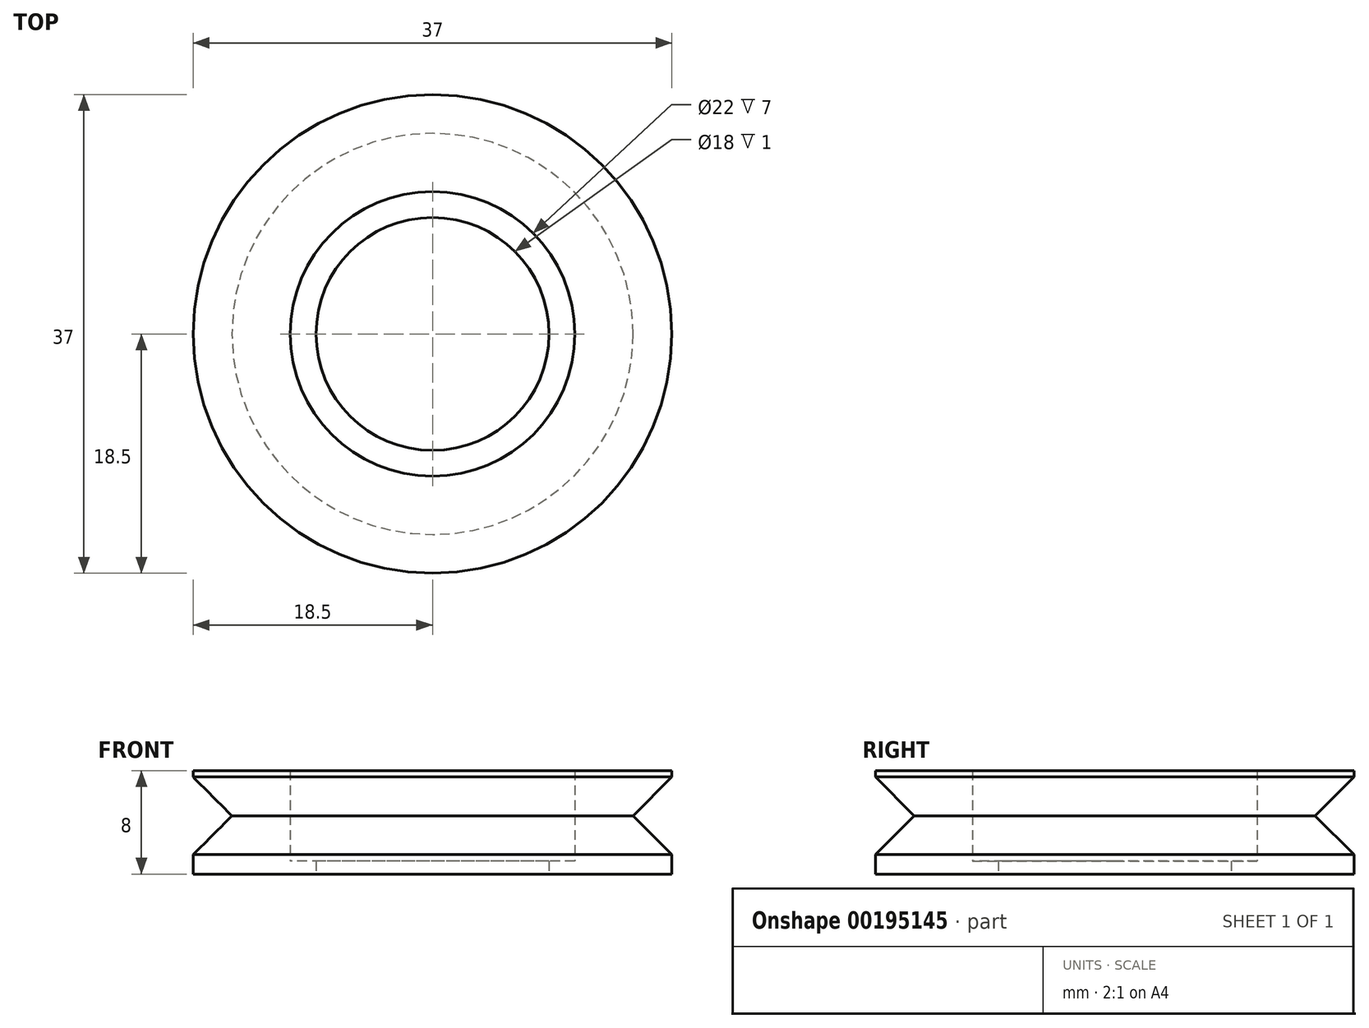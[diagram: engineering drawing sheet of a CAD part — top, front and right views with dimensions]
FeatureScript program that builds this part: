
annotation { "Feature Type Name" : "Feature", "Feature Type Description" : "" }
export const myFeature = defineFeature(function(context is Context, id is Id, definition is map)
    precondition{}
    {
        {
            var Q0;
            Q0=qCreatedBy(makeId("Top.planeOp"),FACE);
            var sketch = newSketch(context, id + "F0", { "sketchPlane" : qUnion([Q0])});
            skCircle(sketch, "E0", {"center": v(0, 0) * mm, "radius": 11 * mm});
            skCircle(sketch, "E1", {"center": v(0, 0) * mm, "radius": 18.5 * mm});
            skSolve(sketch);
        }
        {
            var Q0;
            Q0=makeQuery(id+"F0.imprint","IMPRINT",FACE,{"disambiguationData":[TD([[makeQuery(id+"F0.imprint","IMPRINT",EDGE,{"derivedFrom":sQuery(id+"F0.wireOp",EDGE,"E0")}),-1.0]])]});
            extrude(context, id + "F1", {"entities" : qUnion([Q0]), "depth" : 7 * mm});
        }
        {
            var Q0;
            Q0=makeQuery(id+"F0.imprint","IMPRINT",FACE,{"disambiguationData":[TD([[makeQuery(id+"F0.imprint","IMPRINT",EDGE,{"derivedFrom":sQuery(id+"F0.wireOp",EDGE,"E0")}),1.0]])]});
            var Q1;
            Q1=makeQuery(id+"F0.imprint","IMPRINT",FACE,{"disambiguationData":[TD([[makeQuery(id+"F0.imprint","IMPRINT",EDGE,{"derivedFrom":sQuery(id+"F0.wireOp",EDGE,"E0")}),-1.0]])]});
            extrude(context, id + "F2", {"entities" : qUnion([Q0, Q1]), "operationType" : NewBodyOperationType.ADD, "oppositeDirection" : true, "depth" : 1 * mm});
        }
        {
            var Q0;
            Q0=makeQuery(id+"F2.opExtrude","CAP_FACE",FACE,{"disambiguationData":[OSD([sQuery(id+"F0.wireOp",EDGE,"E1")])],"isStart":false});
            var sketch = newSketch(context, id + "F3", { "sketchPlane" : qUnion([Q0])});
            skCircle(sketch, "E2", {"center": v(0, 0) * mm, "radius": 9 * mm});
            skSolve(sketch);
        }
        {
            var Q0;
            Q0=makeQuery(id+"F3.imprint","IMPRINT",FACE,{"disambiguationData":[TD([[makeQuery(id+"F3.imprint","IMPRINT",EDGE,{"derivedFrom":sQuery(id+"F3.wireOp",EDGE,"E2")}),1.0]])]});
            extrude(context, id + "F4", {"entities" : qUnion([Q0]), "operationType" : NewBodyOperationType.REMOVE, "oppositeDirection" : true, "depth" : 25 * mm});
        }
        {
            var Q0;
            Q0=qCreatedBy(makeId("Front.planeOp"),FACE);
            var sketch = newSketch(context, id + "F5", { "sketchPlane" : qUnion([Q0])});
            skLineSegment(sketch, "E3", {"start": v(0, 8.94) * mm, "end": v(0, -2.8) * mm, "construction": true});
            skLineSegment(sketch, "E4", {"start": v(-18.5, -1) * mm, "end": v(-18.5, 7) * mm});
            skLineSegment(sketch, "E5", {"start": v(-15.5, 3.5) * mm, "end": v(-18.5, 6.5) * mm});
            skLineSegment(sketch, "E6", {"start": v(-15.5, 3.5) * mm, "end": v(-18.5, 0.5) * mm});
            skSolve(sketch);
        }
        {
            var Q0;
            Q0 = qSketchRegion(id + "F5", true);
            var Q1;
            Q1=sQuery(id+"F5.wireOp",EDGE,"E3");
            revolve(context, id + "F6", {"operationType" : NewBodyOperationType.REMOVE, "entities" : qUnion([Q0]), "axis" : qUnion([Q1]), "revolveType" : RevolveType.FULL, "oppositeDirection" : true});
        }
    });
